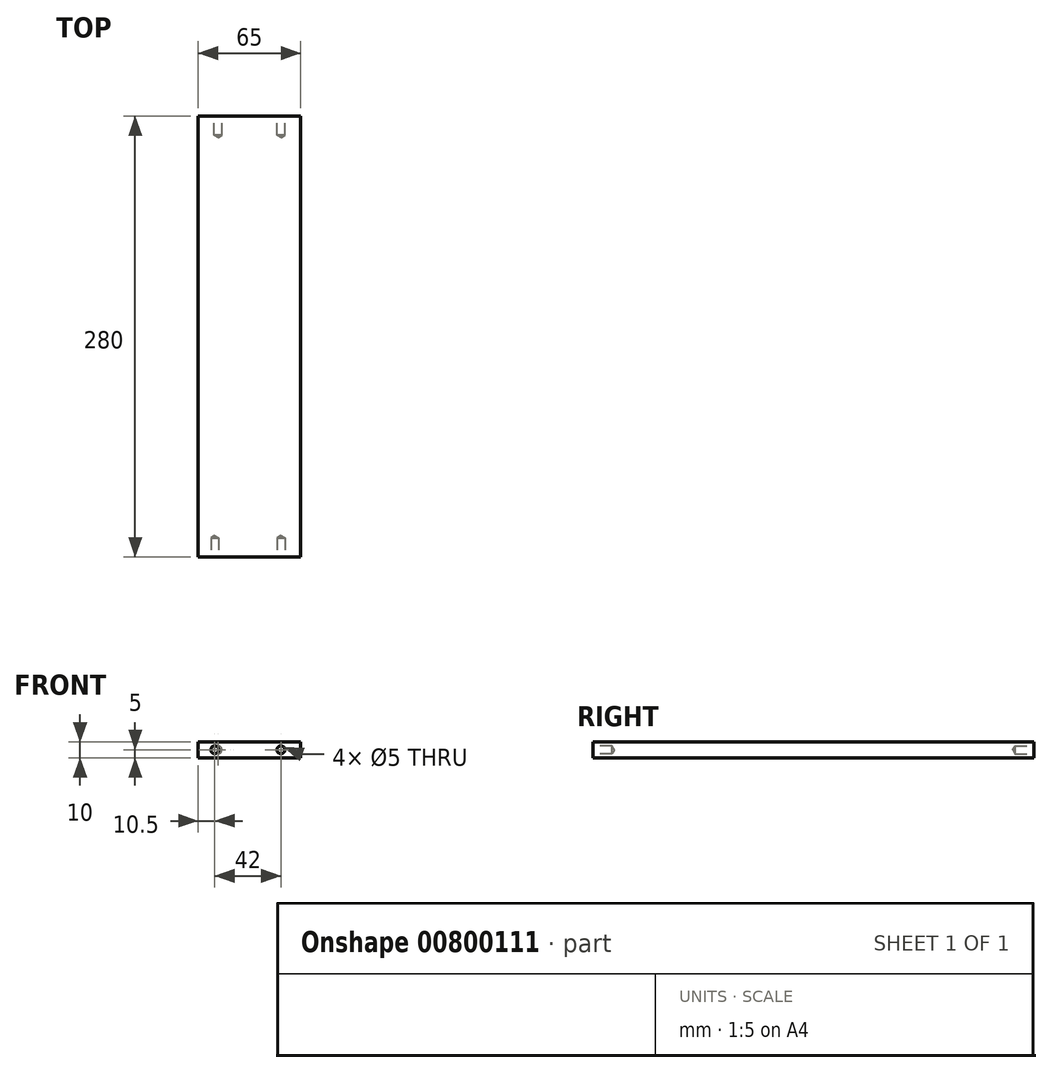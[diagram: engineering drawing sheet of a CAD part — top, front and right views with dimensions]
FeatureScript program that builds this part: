
annotation { "Feature Type Name" : "Feature", "Feature Type Description" : "" }
export const myFeature = defineFeature(function(context is Context, id is Id, definition is map)
    precondition{}
    {
        {
            var Q0;
            Q0=qCreatedBy(makeId("Top.planeOp"),FACE);
            var sketch = newSketch(context, id + "F0", { "sketchPlane" : qUnion([Q0])});
            skLineSegment(sketch, "E0.bottom", {"start": v(-32.5, 140) * mm, "end": v(32.5, 140) * mm});
            skLineSegment(sketch, "E0.top", {"start": v(-32.5, -140) * mm, "end": v(32.5, -140) * mm});
            skLineSegment(sketch, "E0.left", {"start": v(-32.5, 140) * mm, "end": v(-32.5, -140) * mm});
            skLineSegment(sketch, "E0.right", {"start": v(32.5, 140) * mm, "end": v(32.5, -140) * mm});
            skSolve(sketch);
        }
        {
            var Q0;
            Q0=makeQuery(id+"F0.imprint","IMPRINT",FACE,{"disambiguationData":[TD([[makeQuery(id+"F0.imprint","IMPRINT",EDGE,{"derivedFrom":sQuery(id+"F0.wireOp",EDGE,"E0.bottom")}),-1.0]])]});
            extrude(context, id + "F1", {"entities" : qUnion([Q0]), "depth" : 10 * mm, "offsetDistance" : 25 * mm});
        }
        {
            var Q0;
            Q0=qCreatedBy(makeId("Front.planeOp"),FACE);
            cPlane(context, id + "F2", {"entities" : qUnion([Q0]), "cplaneType" : CPlaneType.OFFSET, "offset" : 140 * mm, "width" : 150 * mm, "height" : 150 * mm});
        }
        {
            var Q0;
            Q0=qCreatedBy(id+"F2.planeOp",FACE);
            var sketch = newSketch(context, id + "F3", { "sketchPlane" : qUnion([Q0])});
            skPoint(sketch, "E1", {"position": v(-22, 5) * mm});
            skPoint(sketch, "E2", {"position": v(20, 5) * mm});
            skSolve(sketch);
        }
        {
            var Q0;
            Q0=sQuery(id+"F3.wireOp",VERTEX,"E1");
            var Q1;
            Q1=sQuery(id+"F3.wireOp",VERTEX,"E2");
            var Q2;
            Q2=makeQuery(id+"F1.opExtrude","SWEPT_BODY",BODY,{"disambiguationData":[OSD([sQuery(id+"F0.wireOp",EDGE,"E0.bottom"),sQuery(id+"F0.wireOp",EDGE,"E0.top"),sQuery(id+"F0.wireOp",EDGE,"E0.left"),sQuery(id+"F0.wireOp",EDGE,"E0.right")])]});
            hole(context, id + "F4", {"style" : HoleStyle.SIMPLE, "endStyle" : HoleEndStyle.BLIND, "holeDiameter" : 5 * mm, "majorDiameter" : 5 * mm, "holeDepth" : 12 * mm, "isTappedThrough" : true, "tappedDepth" : 2 * mm, "tapClearance" : 3, "startFromSketch" : true, "locations" : qUnion([Q0, Q1]), "scope" : qUnion([Q2])});
        }
        {
            var Q0;
            Q0=qCreatedBy(makeId("Front.planeOp"),FACE);
            cPlane(context, id + "F5", {"entities" : qUnion([Q0]), "cplaneType" : CPlaneType.OFFSET, "offset" : 140 * mm, "oppositeDirection" : true, "width" : 150 * mm, "height" : 150 * mm});
        }
        {
            var Q0;
            Q0=qCreatedBy(id+"F5.planeOp",FACE);
            var sketch = newSketch(context, id + "F6", { "sketchPlane" : qUnion([Q0])});
            skPoint(sketch, "E3", {"position": v(-20, 5) * mm});
            skPoint(sketch, "E4", {"position": v(20, 5) * mm});
            skSolve(sketch);
        }
        {
            var Q0;
            Q0=sQuery(id+"F6.wireOp",VERTEX,"E3");
            var Q1;
            Q1=sQuery(id+"F6.wireOp",VERTEX,"E4");
            var Q2;
            Q2=makeQuery(id+"F1.opExtrude","SWEPT_BODY",BODY,{"disambiguationData":[OSD([sQuery(id+"F0.wireOp",EDGE,"E0.bottom"),sQuery(id+"F0.wireOp",EDGE,"E0.top"),sQuery(id+"F0.wireOp",EDGE,"E0.left"),sQuery(id+"F0.wireOp",EDGE,"E0.right")])]});
            hole(context, id + "F7", {"style" : HoleStyle.SIMPLE, "endStyle" : HoleEndStyle.BLIND, "oppositeDirection" : true, "holeDiameter" : 5 * mm, "majorDiameter" : 5 * mm, "holeDepth" : 12 * mm, "isTappedThrough" : true, "tappedDepth" : 2 * mm, "tapClearance" : 3, "startFromSketch" : true, "locations" : qUnion([Q0, Q1]), "scope" : qUnion([Q2])});
        }
    });
